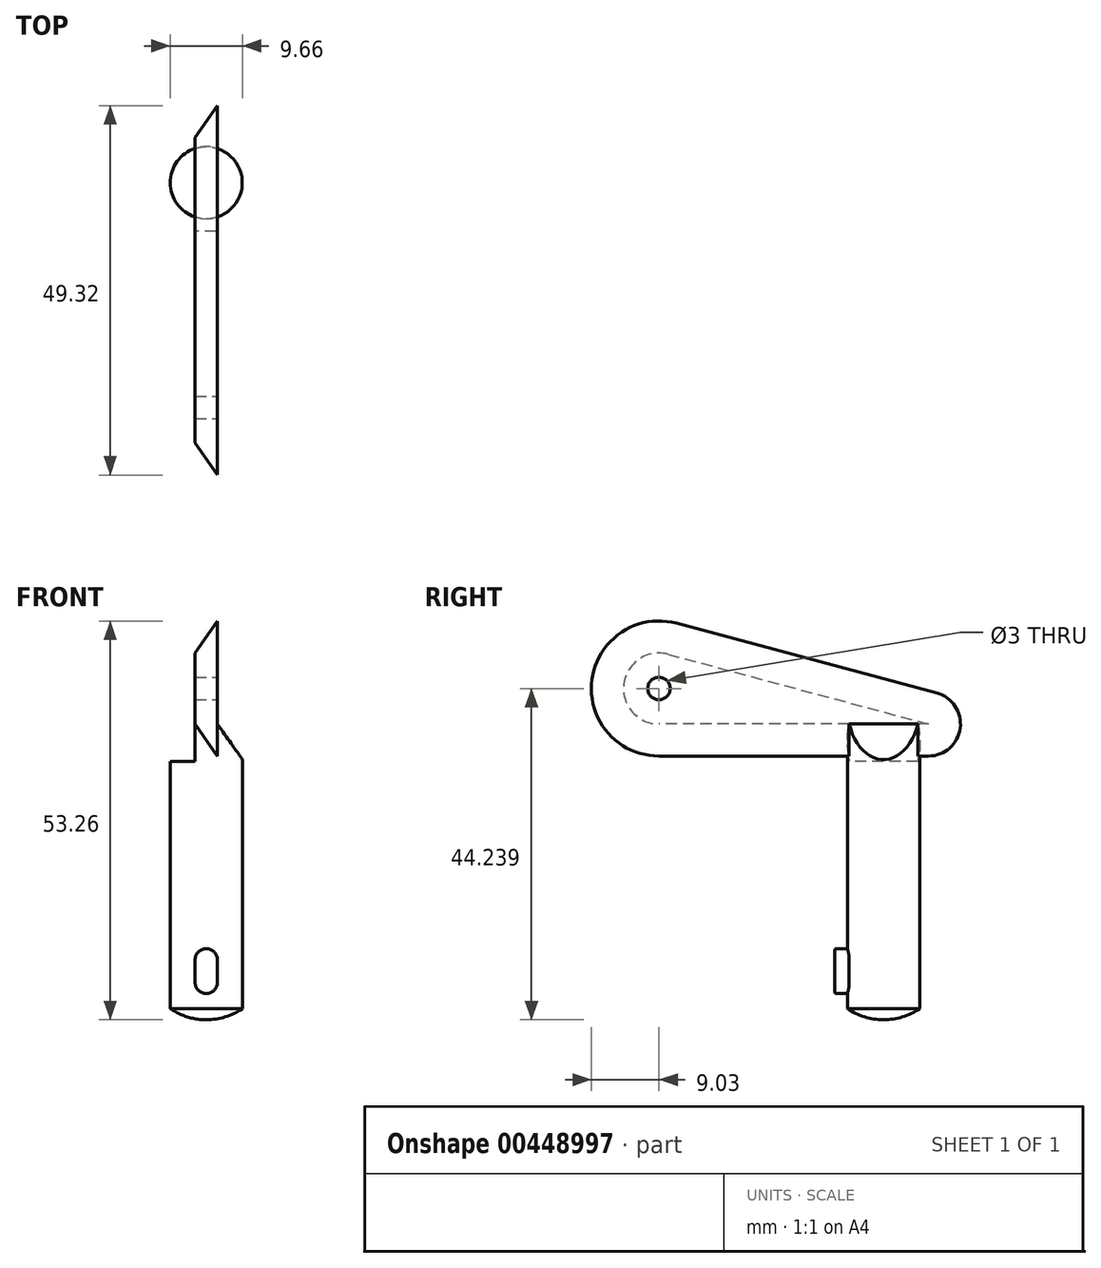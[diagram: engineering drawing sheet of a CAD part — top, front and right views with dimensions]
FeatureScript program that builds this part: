
annotation { "Feature Type Name" : "Feature", "Feature Type Description" : "" }
export const myFeature = defineFeature(function(context is Context, id is Id, definition is map)
    precondition{}
    {
        {
            var Q0;
            Q0=qCreatedBy(makeId("Top.planeOp"),FACE);
            var sketch = newSketch(context, id + "F0", { "sketchPlane" : qUnion([Q0])});
            skCircle(sketch, "E0", {"center": v(0, 0) * mm, "radius": 4.83 * mm});
            skSolve(sketch);
        }
        {
            var Q0;
            Q0=qSketchRegion(id+"F0",true);
            extrude(context, id + "F1", {"entities" : qUnion([Q0]), "depth" : 33 * mm});
        }
        {
            var Q0;
            Q0=qCreatedBy(makeId("Front.planeOp"),FACE);
            var sketch = newSketch(context, id + "F2", { "sketchPlane" : qUnion([Q0])});
            skLineSegment(sketch, "E1", {"start": v(0, 3.5) * mm, "end": v(0, 6.5) * mm, "construction": true});
            skArc(sketch, "E2.0.startCap", {"start": v(1.5, 3.5) * mm, "mid": v(0, 2) * mm, "end": v(-1.5, 3.5) * mm});
            skArc(sketch, "E2.0.endCap", {"start": v(-1.5, 6.5) * mm, "mid": v(0, 8) * mm, "end": v(1.5, 6.5) * mm});
            skLineSegment(sketch, "E2.0.left", {"start": v(-1.5, 3.5) * mm, "end": v(-1.5, 6.5) * mm});
            skLineSegment(sketch, "E2.0.right", {"start": v(1.5, 3.5) * mm, "end": v(1.5, 6.5) * mm});
            skSolve(sketch);
        }
        {
            var Q0;
            Q0=qSketchRegion(id+"F2",true);
            var Q1;
            Q1=qBodyType(qCreatedBy(id+"F2",EDGE),BodyType.WIRE);
            extrude(context, id + "F3", {"entities" : qUnion([Q0]), "operationType" : NewBodyOperationType.ADD, "surfaceEntities" : qUnion([Q1]), "depth" : 6.5 * mm});
        }
        {
            var Q0;
            Q0=makeQuery(id+"F3.opExtrude","CAP_FACE",FACE,{"disambiguationData":[OSD([sQuery(id+"F2.wireOp",EDGE,"E2.0.startCap"),sQuery(id+"F2.wireOp",EDGE,"E2.0.endCap"),sQuery(id+"F2.wireOp",EDGE,"E2.0.left"),sQuery(id+"F2.wireOp",EDGE,"E2.0.right")])],"isStart":false});
            fillet(context, id + "F4", {"entities" : qUnion([Q0]), "radius" : 0.2 * mm, "tangentPropagation" : true, "allowEdgeOverflow" : false});
        }
        {
            var Q0;
            Q0=qCreatedBy(makeId("Front.planeOp"),FACE);
            var sketch = newSketch(context, id + "F5", { "sketchPlane" : qUnion([Q0])});
            skLineSegment(sketch, "E3", {"start": v(0, 0) * mm, "end": v(0, -2.82) * mm, "construction": true});
            skLineSegment(sketch, "E4", {"start": v(-4.62, -1.5) * mm, "end": v(4.9, -1.5) * mm, "construction": true});
            skLineSegment(sketch, "E5.0", {"start": v(-4.83, 0) * mm, "end": v(0, 0) * mm});
            skArc(sketch, "E6", {"start": v(-4.83, 0) * mm, "mid": v(-2.53, -1.12) * mm, "end": v(0, -1.5) * mm});
            skLineSegment(sketch, "E7", {"start": v(0, 0) * mm, "end": v(0, -1.5) * mm});
            skPoint(sketch, "E8.orphan", {"position": v(4.83, 0) * mm});
            skSolve(sketch);
        }
        {
            var Q0;
            Q0=qSketchRegion(id+"F5",true);
            var Q1;
            Q1=sQuery(id+"F5.wireOp",EDGE,"E3");
            revolve(context, id + "F6", {"operationType" : NewBodyOperationType.ADD, "entities" : qUnion([Q0]), "axis" : qUnion([Q1]), "revolveType" : RevolveType.FULL});
        }
        {
            var Q0;
            Q0=qCreatedBy(makeId("Right.planeOp"),FACE);
            var sketch = newSketch(context, id + "F7", { "sketchPlane" : qUnion([Q0])});
            skLineSegment(sketch, "E9.MirrorCS", {"start": v(7.3, 42.83) * mm, "end": v(-27.48, 52.15) * mm});
            skArc(sketch, "E10.MirrorCS", {"start": v(-30, 33) * mm, "mid": v(-39.66, 44.01) * mm, "end": v(-27.48, 52.15) * mm});
            skLineSegment(sketch, "E11.MirrorCS", {"start": v(-6, 33) * mm, "end": v(-30, 33) * mm});
            skArc(sketch, "E12.MirrorCS", {"start": v(7.3, 42.83) * mm, "mid": v(10.96, 37.35) * mm, "end": v(6, 33) * mm});
            skLineSegment(sketch, "E13", {"start": v(-6, 33) * mm, "end": v(6, 33) * mm});
            skPoint(sketch, "E14", {"position": v(0, 33) * mm});
            skLineSegment(sketch, "E15", {"start": v(6, 38) * mm, "end": v(-30, 42.74) * mm, "construction": true});
            skSolve(sketch);
        }
        {
            var Q0;
            Q0 = qSketchRegion(id + "F7", true);
            extrude(context, id + "F8", {"entities" : qUnion([Q0]), "operationType" : NewBodyOperationType.ADD, "depth" : 1.5 * mm, "offsetDistance" : 25 * mm, "hasSecondDirection" : true, "secondDirectionOppositeDirection" : true, "secondDirectionDepth" : 1.5 * mm});
        }
        {
            var Q0;
            {var subQ0=sQuery(id+"F7.wireOp",EDGE,"E13");var subQ1=sQuery(id+"F7.wireOp",EDGE,"E11.MirrorCS");Q0=makeQuery(id+"F8.boolean.opBoolean","SPLIT",EDGE,{"disambiguationData":[topologyDisambiguationEdgeConnected([makeQuery(id+"F1.opExtrude","CAP_FACE",FACE,{"disambiguationData":[OSD([sQuery(id+"F0.wireOp",EDGE,"E0")])],"isStart":false}),makeQuery(id+"F8.opExtrude","CAP_FACE",FACE,{"disambiguationData":[OSD([sQuery(id+"F7.wireOp",EDGE,"E9.MirrorCS"),sQuery(id+"F7.wireOp",EDGE,"E10.MirrorCS"),subQ1,sQuery(id+"F7.wireOp",EDGE,"E12.MirrorCS"),subQ0])],"isStart":false})])],"derivedFrom":makeQuery(id+"F8.opExtrude","CAP_EDGE",EDGE,{"disambiguationData":[OSD([subQ1,subQ0])],"isStart":false})});}
            chamfer(context, id + "F9", {"entities" : qUnion([Q0]), "chamferType" : ChamferType.TWO_OFFSETS, "width1" : 3.5 * mm, "oppositeDirection" : false, "width2" : 5 * mm, "tangentPropagation" : true});
        }
        {
            var Q0;
            {var subQ0=sQuery(id+"F7.wireOp",EDGE,"E13");var subQ1=sQuery(id+"F7.wireOp",EDGE,"E11.MirrorCS");Q0=makeQuery(id+"F8.boolean.opBoolean","SPLIT",EDGE,{"disambiguationData":[topologyDisambiguationEdgeConnected([makeQuery(id+"F1.opExtrude","CAP_FACE",FACE,{"disambiguationData":[OSD([sQuery(id+"F0.wireOp",EDGE,"E0")])],"isStart":false}),makeQuery(id+"F8.opExtrude","CAP_FACE",FACE,{"disambiguationData":[OSD([sQuery(id+"F7.wireOp",EDGE,"E9.MirrorCS"),sQuery(id+"F7.wireOp",EDGE,"E10.MirrorCS"),subQ1,sQuery(id+"F7.wireOp",EDGE,"E12.MirrorCS"),subQ0])],"isStart":true})])],"derivedFrom":makeQuery(id+"F8.opExtrude","CAP_EDGE",EDGE,{"disambiguationData":[OSD([subQ1,subQ0])],"isStart":true})});}
            chamfer(context, id + "F10", {"entities" : qUnion([Q0]), "chamferType" : ChamferType.TWO_OFFSETS, "width1" : 3.5 * mm, "oppositeDirection" : true, "width2" : 5 * mm, "tangentPropagation" : true});
        }
        {
            var Q0;
            Q0=makeQuery(id+"F8.opExtrude","CAP_FACE",FACE,{"disambiguationData":[OSD([sQuery(id+"F7.wireOp",EDGE,"E9.MirrorCS"),sQuery(id+"F7.wireOp",EDGE,"E10.MirrorCS"),sQuery(id+"F7.wireOp",EDGE,"E11.MirrorCS"),sQuery(id+"F7.wireOp",EDGE,"E12.MirrorCS"),sQuery(id+"F7.wireOp",EDGE,"E13")])],"isStart":false});
            var sketch = newSketch(context, id + "F11", { "sketchPlane" : qUnion([Q0])});
            skPoint(sketch, "E16.0", {"position": v(-30, 42.74) * mm});
            skCircle(sketch, "E17", {"center": v(-30, 42.74) * mm, "radius": 1.5 * mm});
            skSolve(sketch);
        }
        {
            var Q0;
            Q0 = qSketchRegion(id + "F11", true);
            extrude(context, id + "F12", {"entities" : qUnion([Q0]), "operationType" : NewBodyOperationType.REMOVE, "endBound" : BoundingType.THROUGH_ALL, "oppositeDirection" : true, "depth" : 25 * mm, "offsetDistance" : 25 * mm});
        }
    });
